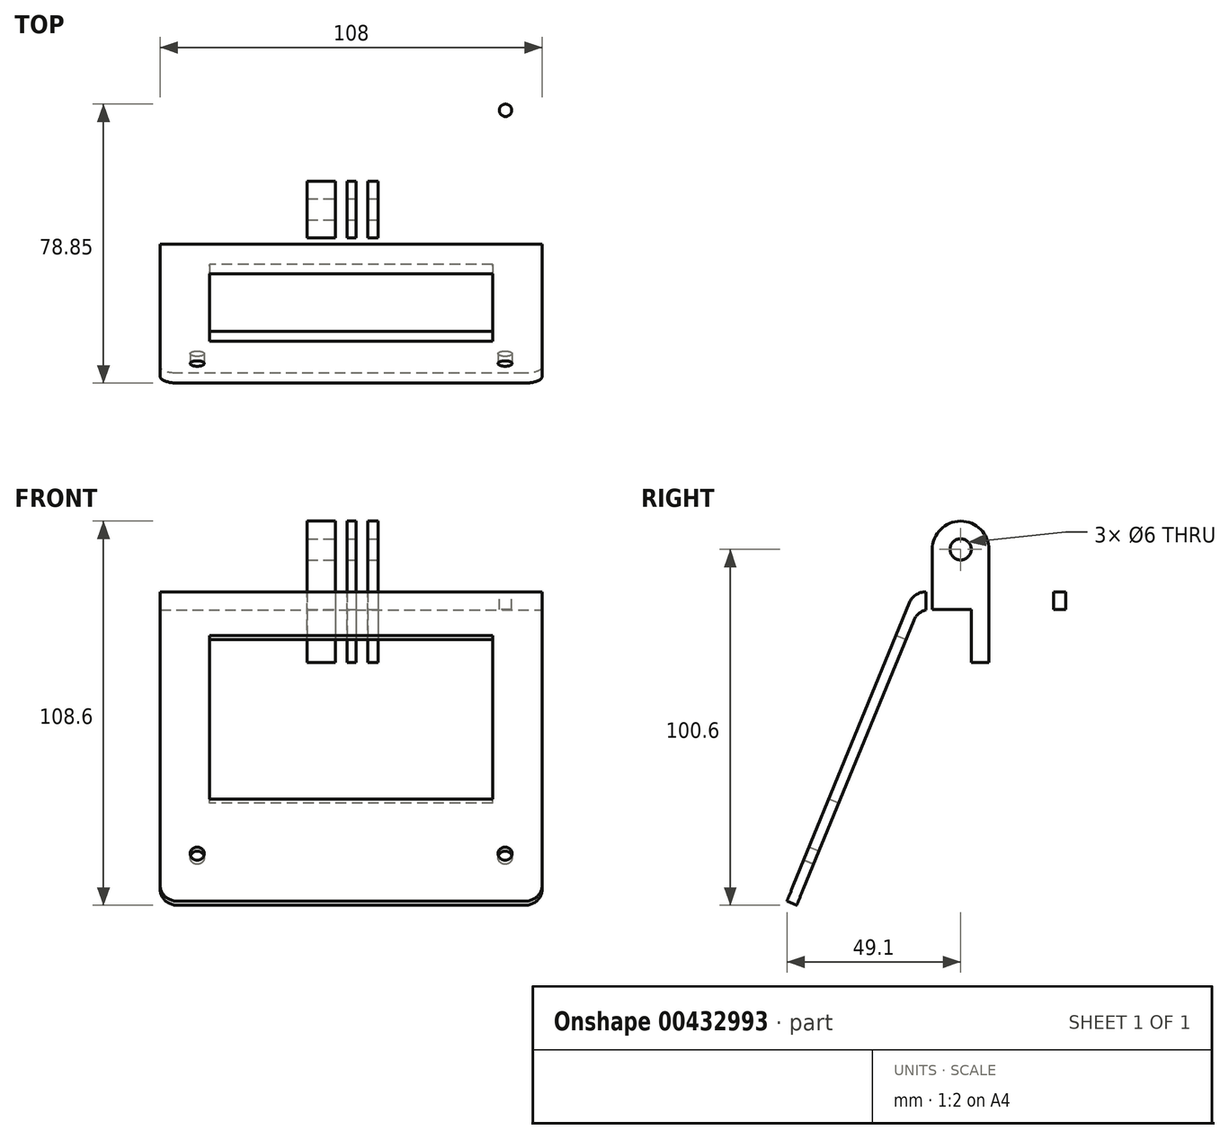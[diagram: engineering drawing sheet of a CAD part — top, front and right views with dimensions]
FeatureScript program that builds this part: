
annotation { "Feature Type Name" : "Feature", "Feature Type Description" : "" }
export const myFeature = defineFeature(function(context is Context, id is Id, definition is map)
    precondition{}
    {
        {
            var Q0;
            Q0=qCreatedBy(makeId("Top.planeOp"),FACE);
            var sketch = newSketch(context, id + "F0", { "sketchPlane" : qUnion([Q0])});
            skLineSegment(sketch, "E0.bottom", {"start": v(-54, 30) * mm, "end": v(-32.5, 30) * mm});
            skLineSegment(sketch, "E0.top", {"start": v(-54, 0) * mm, "end": v(-32.5, 0) * mm});
            skLineSegment(sketch, "E0.left", {"start": v(-54, 30) * mm, "end": v(-54, 0) * mm});
            skLineSegment(sketch, "E0.right", {"start": v(-32.5, 30) * mm, "end": v(-32.5, 0) * mm});
            skLineSegment(sketch, "E1.bottom", {"start": v(32.5, 30) * mm, "end": v(54, 30) * mm});
            skLineSegment(sketch, "E1.top", {"start": v(32.5, 0) * mm, "end": v(54, 0) * mm});
            skLineSegment(sketch, "E1.left", {"start": v(54, 30) * mm, "end": v(54, 0) * mm});
            skLineSegment(sketch, "E1.right", {"start": v(32.5, 30) * mm, "end": v(32.5, 0) * mm});
            skLineSegment(sketch, "E2.bottom", {"start": v(-54, 0) * mm, "end": v(32.5, 0) * mm});
            skLineSegment(sketch, "E3.bottom", {"start": v(-54, 0) * mm, "end": v(54, 0) * mm});
            skLineSegment(sketch, "E3.top", {"start": v(-54, -20) * mm, "end": v(54, -20) * mm});
            skLineSegment(sketch, "E3.left", {"start": v(-54, 0) * mm, "end": v(-54, -20) * mm});
            skLineSegment(sketch, "E3.right", {"start": v(54, 0) * mm, "end": v(54, -20) * mm});
            skSolve(sketch);
        }
        {
            var Q0;
            Q0=makeQuery(id+"F0.imprint","IMPRINT",FACE,{"disambiguationData":[TD([[makeQuery(id+"F0.imprint","IMPRINT",EDGE,{"derivedFrom":sQuery(id+"F0.wireOp",EDGE,"E0.bottom")}),-1.0]])]});
            var Q1;
            Q1=makeQuery(id+"F0.imprint","IMPRINT",FACE,{"disambiguationData":[TD([[makeQuery(id+"F0.imprint","IMPRINT",EDGE,{"derivedFrom":sQuery(id+"F0.wireOp",EDGE,"E3.top")}),1.0]])]});
            var Q2;
            Q2=makeQuery(id+"F0.imprint","IMPRINT",FACE,{"disambiguationData":[TD([[makeQuery(id+"F0.imprint","IMPRINT",EDGE,{"derivedFrom":sQuery(id+"F0.wireOp",EDGE,"E1.bottom")}),-1.0]])]});
            extrude(context, id + "F1", {"entities" : qUnion([Q0, Q1, Q2]), "depth" : 5 * mm});
        }
        {
            var Q0;
            Q0=makeQuery(id+"F1.opExtrude","SWEPT_FACE",FACE,{"disambiguationData":[OSD([sQuery(id+"F0.wireOp",EDGE,"E0.left"),sQuery(id+"F0.wireOp",EDGE,"E3.left")])]});
            var sketch = newSketch(context, id + "F2", { "sketchPlane" : qUnion([Q0])});
            skLineSegment(sketch, "E4", {"start": v(20, 0) * mm, "end": v(54.33, -83.6) * mm});
            skLineSegment(sketch, "E5", {"start": v(54.33, -83.6) * mm, "end": v(57.1, -82.46) * mm});
            skLineSegment(sketch, "E6", {"start": v(57.1, -82.46) * mm, "end": v(21.2, 5) * mm});
            skLineSegment(sketch, "E7", {"start": v(21.2, 5) * mm, "end": v(20, 5) * mm});
            skSolve(sketch);
        }
        {
            var Q0;
            Q0=makeQuery(id+"F2.imprint","IMPRINT",FACE,{"disambiguationData":[TD([[makeQuery(id+"F2.imprint","IMPRINT",EDGE,{"derivedFrom":sQuery(id+"F2.wireOp",EDGE,"E4")}),1.0]])]});
            extrude(context, id + "F3", {"entities" : qUnion([Q0]), "operationType" : NewBodyOperationType.ADD, "oppositeDirection" : true, "depth" : 108 * mm});
        }
        {
            var Q0;
            Q0=makeQuery(id+"F3.opExtrude","SWEPT_FACE",FACE,{"disambiguationData":[OSD([sQuery(id+"F2.wireOp",EDGE,"E6")])]});
            var sketch = newSketch(context, id + "F4", { "sketchPlane" : qUnion([Q0])});
            skLineSegment(sketch, "E8", {"start": v(-64.47, -83.42) * mm, "end": v(61.14, -83.42) * mm, "construction": true});
            skCircle(sketch, "E9", {"center": v(-43.5, -83.42) * mm, "radius": 2 * mm});
            skCircle(sketch, "E10", {"center": v(43.5, -83.42) * mm, "radius": 2 * mm});
            skSolve(sketch);
        }
        {
            var Q0;
            Q0=makeQuery(id+"F4.imprint","IMPRINT",FACE,{"disambiguationData":[TD([[makeQuery(id+"F4.imprint","IMPRINT",EDGE,{"derivedFrom":sQuery(id+"F4.wireOp",EDGE,"E9")}),1.0]])]});
            var Q1;
            Q1=makeQuery(id+"F4.imprint","IMPRINT",FACE,{"disambiguationData":[TD([[makeQuery(id+"F4.imprint","IMPRINT",EDGE,{"derivedFrom":sQuery(id+"F4.wireOp",EDGE,"E10")}),1.0]])]});
            extrude(context, id + "F5", {"entities" : qUnion([Q0, Q1]), "operationType" : NewBodyOperationType.REMOVE, "oppositeDirection" : true, "depth" : 25 * mm});
        }
        {
            var Q0;
            Q0=makeQuery(id+"F3.boolean.opBoolean","MERGE",FACE,{"derivedFrom":[makeQuery(id+"F1.opExtrude","CAP_FACE",FACE,{"disambiguationData":[OSD([sQuery(id+"F0.wireOp",EDGE,"E0.bottom"),sQuery(id+"F0.wireOp",EDGE,"E0.left"),sQuery(id+"F0.wireOp",EDGE,"E0.right"),sQuery(id+"F0.wireOp",EDGE,"E1.bottom"),sQuery(id+"F0.wireOp",EDGE,"E1.left"),sQuery(id+"F0.wireOp",EDGE,"E1.right"),sQuery(id+"F0.wireOp",EDGE,"E3.bottom"),sQuery(id+"F0.wireOp",EDGE,"E3.top"),sQuery(id+"F0.wireOp",EDGE,"E3.left"),sQuery(id+"F0.wireOp",EDGE,"E3.right")])],"isStart":false}),makeQuery(id+"F3.opExtrude","SWEPT_FACE",FACE,{"disambiguationData":[OSD([sQuery(id+"F2.wireOp",EDGE,"E7")])]})]});
            var sketch = newSketch(context, id + "F6", { "sketchPlane" : qUnion([Q0])});
            skLineSegment(sketch, "E11.bottom", {"start": v(-20, 0) * mm, "end": v(20, 0) * mm});
            skLineSegment(sketch, "E11.top", {"start": v(-20, -21.2) * mm, "end": v(20, -21.2) * mm});
            skLineSegment(sketch, "E11.left", {"start": v(-20, 0) * mm, "end": v(-20, -21.2) * mm});
            skLineSegment(sketch, "E11.right", {"start": v(20, 0) * mm, "end": v(20, -21.2) * mm});
            skLineSegment(sketch, "E12.bottom", {"start": v(-20, 0) * mm, "end": v(-12.45, 0) * mm});
            skLineSegment(sketch, "E12.top", {"start": v(-20, -21.2) * mm, "end": v(-12.45, -21.2) * mm});
            skLineSegment(sketch, "E12.right", {"start": v(-12.45, 0) * mm, "end": v(-12.45, -21.2) * mm});
            skLineSegment(sketch, "E13.bottom", {"start": v(-12.45, 0) * mm, "end": v(-4.45, 0) * mm});
            skLineSegment(sketch, "E13.top", {"start": v(-12.45, -21.2) * mm, "end": v(-4.45, -21.2) * mm});
            skLineSegment(sketch, "E13.right", {"start": v(-4.45, 0) * mm, "end": v(-4.45, -21.2) * mm});
            skLineSegment(sketch, "E14.bottom", {"start": v(-4.45, 0) * mm, "end": v(-1.15, 0) * mm});
            skLineSegment(sketch, "E14.top", {"start": v(-4.45, -21.2) * mm, "end": v(-1.15, -21.2) * mm});
            skLineSegment(sketch, "E14.right", {"start": v(-1.15, 0) * mm, "end": v(-1.15, -21.2) * mm});
            skLineSegment(sketch, "E15.bottom", {"start": v(-1.15, 0) * mm, "end": v(1.35, 0) * mm});
            skLineSegment(sketch, "E15.top", {"start": v(-1.15, -21.2) * mm, "end": v(1.35, -21.2) * mm});
            skLineSegment(sketch, "E15.right", {"start": v(1.35, 0) * mm, "end": v(1.35, -21.2) * mm});
            skLineSegment(sketch, "E16.bottom", {"start": v(1.35, 0) * mm, "end": v(4.65, 0) * mm});
            skLineSegment(sketch, "E16.top", {"start": v(1.35, -21.2) * mm, "end": v(4.65, -21.2) * mm});
            skLineSegment(sketch, "E16.right", {"start": v(4.65, 0) * mm, "end": v(4.65, -21.2) * mm});
            skLineSegment(sketch, "E17.bottom", {"start": v(4.65, 0) * mm, "end": v(7.65, 0) * mm});
            skLineSegment(sketch, "E17.top", {"start": v(4.65, -21.2) * mm, "end": v(7.65, -21.2) * mm});
            skLineSegment(sketch, "E17.right", {"start": v(7.65, 0) * mm, "end": v(7.65, -21.2) * mm});
            skLineSegment(sketch, "E18.top", {"start": v(-20, -16) * mm, "end": v(20, -16) * mm});
            skLineSegment(sketch, "E18.left", {"start": v(-20, 0) * mm, "end": v(-20, -16) * mm});
            skLineSegment(sketch, "E18.right", {"start": v(20, 0) * mm, "end": v(20, -16) * mm});
            skSolve(sketch);
        }
        {
            var Q0;
            Q0=makeQuery(id+"F3.opExtrude","SWEPT_EDGE",EDGE,{"disambiguationData":[OSD([sQuery(id+"F2.wireOp",EDGE,"E6"),sQuery(id+"F2.wireOp",EDGE,"E7")])]});
            var Q1;
            {var subQ0=sQuery(id+"F0.wireOp",EDGE,"E3.top");Q1=makeQuery(id+"F3.boolean.opBoolean","MERGE",EDGE,{"derivedFrom":[makeQuery(id+"F1.opExtrude","CAP_EDGE",EDGE,{"disambiguationData":[OSD([subQ0])],"isStart":true}),makeQuery(id+"F3.opExtrude","SWEPT_EDGE",EDGE,{"disambiguationData":[OSD([sQuery(id+"F0.wireOp",EDGE,"E0.left"),subQ0,sQuery(id+"F0.wireOp",EDGE,"E3.left"),sQuery(id+"F2.wireOp",EDGE,"E4")])]})]});}
            var Q2;
            Q2=makeQuery(id+"F1.opExtrude","SWEPT_EDGE",EDGE,{"disambiguationData":[OSD([sQuery(id+"F0.wireOp",EDGE,"E0.bottom"),sQuery(id+"F0.wireOp",EDGE,"E0.left")])]});
            var Q3;
            Q3=makeQuery(id+"F1.opExtrude","SWEPT_EDGE",EDGE,{"disambiguationData":[OSD([sQuery(id+"F0.wireOp",EDGE,"E1.bottom"),sQuery(id+"F0.wireOp",EDGE,"E1.left")])]});
            var Q4;
            Q4=makeQuery(id+"F3.opExtrude","CAP_EDGE",EDGE,{"disambiguationData":[OSD([sQuery(id+"F2.wireOp",EDGE,"E5")])],"isStart":false});
            var Q5;
            Q5=makeQuery(id+"F3.opExtrude","CAP_EDGE",EDGE,{"disambiguationData":[OSD([sQuery(id+"F2.wireOp",EDGE,"E5")])],"isStart":true});
            var Q6;
            Q6=makeQuery(id+"F1.opExtrude","SWEPT_EDGE",EDGE,{"disambiguationData":[OSD([sQuery(id+"F0.wireOp",EDGE,"E0.right"),sQuery(id+"F0.wireOp",EDGE,"E3.bottom")])]});
            var Q7;
            Q7=makeQuery(id+"F1.opExtrude","SWEPT_EDGE",EDGE,{"disambiguationData":[OSD([sQuery(id+"F0.wireOp",EDGE,"E1.right"),sQuery(id+"F0.wireOp",EDGE,"E3.bottom")])]});
            fillet(context, id + "F7", {"entities" : qUnion([Q0, Q1, Q2, Q3, Q4, Q5, Q6, Q7]), "radius" : 5 * mm, "tangentPropagation" : true, "allowEdgeOverflow" : false});
        }
        {
            var Q0;
            {var subQ0=sQuery(id+"F6.wireOp",EDGE,"E11.bottom");var subQ1=sQuery(id+"F6.wireOp",EDGE,"E12.right");var subQ2=makeQuery(id+"F6.imprint","INTERSECT",VERTEX,{"derivedFrom":[subQ1,subQ0]});Q0=makeQuery(id+"F6.imprint","IMPRINT",FACE,{"disambiguationData":[TD([[makeQuery(id+"F6.imprint","IMPRINT",EDGE,{"disambiguationData":[TD([[subQ2,-1.0]])],"derivedFrom":subQ1}),1.0]])]});}
            var Q1;
            {var subQ0=sQuery(id+"F6.wireOp",EDGE,"E11.bottom");var subQ1=sQuery(id+"F6.wireOp",EDGE,"E14.right");var subQ2=makeQuery(id+"F6.imprint","INTERSECT",VERTEX,{"derivedFrom":[subQ1,subQ0]});Q1=makeQuery(id+"F6.imprint","IMPRINT",FACE,{"disambiguationData":[TD([[makeQuery(id+"F6.imprint","IMPRINT",EDGE,{"disambiguationData":[TD([[subQ2,-1.0]])],"derivedFrom":subQ1}),1.0]])]});}
            var Q2;
            {var subQ0=sQuery(id+"F6.wireOp",EDGE,"E11.bottom");var subQ1=sQuery(id+"F6.wireOp",EDGE,"E16.right");var subQ2=makeQuery(id+"F6.imprint","INTERSECT",VERTEX,{"derivedFrom":[subQ1,subQ0]});Q2=makeQuery(id+"F6.imprint","IMPRINT",FACE,{"disambiguationData":[TD([[makeQuery(id+"F6.imprint","IMPRINT",EDGE,{"disambiguationData":[TD([[subQ2,-1.0]])],"derivedFrom":subQ1}),1.0]])]});}
            extrude(context, id + "F8", {"entities" : qUnion([Q0, Q1, Q2]), "operationType" : NewBodyOperationType.ADD, "depth" : 20 * mm});
        }
        {
            var Q0;
            {var subQ0=sQuery(id+"F6.wireOp",EDGE,"E18.top");Q0=makeQuery(id+"F8.opExtrude","CAP_EDGE",EDGE,{"disambiguationData":[OSD([subQ0]),TDD([makeQuery(id+"F6.imprint","IMPRINT",EDGE,{"disambiguationData":[TD([[makeQuery(id+"F6.imprint","INTERSECT",VERTEX,{"derivedFrom":[sQuery(id+"F6.wireOp",EDGE,"E12.right"),subQ0]}),-1.0]])],"derivedFrom":subQ0})])],"isStart":false});}
            var Q1;
            {var subQ0=sQuery(id+"F6.wireOp",EDGE,"E18.top");Q1=makeQuery(id+"F8.opExtrude","CAP_EDGE",EDGE,{"disambiguationData":[OSD([subQ0]),TDD([makeQuery(id+"F6.imprint","IMPRINT",EDGE,{"disambiguationData":[TD([[makeQuery(id+"F6.imprint","INTERSECT",VERTEX,{"derivedFrom":[sQuery(id+"F6.wireOp",EDGE,"E14.right"),subQ0]}),-1.0]])],"derivedFrom":subQ0})])],"isStart":false});}
            var Q2;
            {var subQ0=sQuery(id+"F6.wireOp",EDGE,"E18.top");Q2=makeQuery(id+"F8.opExtrude","CAP_EDGE",EDGE,{"disambiguationData":[OSD([subQ0]),TDD([makeQuery(id+"F6.imprint","IMPRINT",EDGE,{"disambiguationData":[TD([[makeQuery(id+"F6.imprint","INTERSECT",VERTEX,{"derivedFrom":[sQuery(id+"F6.wireOp",EDGE,"E16.right"),subQ0]}),-1.0]])],"derivedFrom":subQ0})])],"isStart":false});}
            var Q3;
            {var subQ0=sQuery(id+"F6.wireOp",EDGE,"E11.bottom");Q3=makeQuery(id+"F8.opExtrude","CAP_EDGE",EDGE,{"disambiguationData":[OSD([subQ0]),TDD([makeQuery(id+"F6.imprint","IMPRINT",EDGE,{"disambiguationData":[TD([[makeQuery(id+"F6.imprint","INTERSECT",VERTEX,{"derivedFrom":[sQuery(id+"F6.wireOp",EDGE,"E12.right"),subQ0]}),-1.0]])],"derivedFrom":subQ0})])],"isStart":false});}
            var Q4;
            {var subQ0=sQuery(id+"F6.wireOp",EDGE,"E11.bottom");Q4=makeQuery(id+"F8.opExtrude","CAP_EDGE",EDGE,{"disambiguationData":[OSD([subQ0]),TDD([makeQuery(id+"F6.imprint","IMPRINT",EDGE,{"disambiguationData":[TD([[makeQuery(id+"F6.imprint","INTERSECT",VERTEX,{"derivedFrom":[sQuery(id+"F6.wireOp",EDGE,"E14.right"),subQ0]}),-1.0]])],"derivedFrom":subQ0})])],"isStart":false});}
            var Q5;
            {var subQ0=sQuery(id+"F6.wireOp",EDGE,"E11.bottom");Q5=makeQuery(id+"F8.opExtrude","CAP_EDGE",EDGE,{"disambiguationData":[OSD([subQ0]),TDD([makeQuery(id+"F6.imprint","IMPRINT",EDGE,{"disambiguationData":[TD([[makeQuery(id+"F6.imprint","INTERSECT",VERTEX,{"derivedFrom":[sQuery(id+"F6.wireOp",EDGE,"E16.right"),subQ0]}),-1.0]])],"derivedFrom":subQ0})])],"isStart":false});}
            fillet(context, id + "F9", {"entities" : qUnion([Q0, Q1, Q2, Q3, Q4, Q5]), "radius" : 8 * mm, "tangentPropagation" : true, "allowEdgeOverflow" : false});
        }
        {
            var Q0;
            Q0=makeQuery(id+"F8.opExtrude","SWEPT_FACE",FACE,{"disambiguationData":[OSD([sQuery(id+"F6.wireOp",EDGE,"E17.right")])]});
            var sketch = newSketch(context, id + "F10", { "sketchPlane" : qUnion([Q0])});
            skCircle(sketch, "E19", {"center": v(-8, 17) * mm, "radius": 3 * mm});
            skSolve(sketch);
        }
        {
            var Q0;
            Q0=makeQuery(id+"F10.imprint","IMPRINT",FACE,{"disambiguationData":[TD([[makeQuery(id+"F10.imprint","IMPRINT",EDGE,{"derivedFrom":sQuery(id+"F10.wireOp",EDGE,"E19")}),1.0]])]});
            extrude(context, id + "F11", {"entities" : qUnion([Q0]), "operationType" : NewBodyOperationType.REMOVE, "oppositeDirection" : true, "depth" : 40 * mm});
        }
        {
            var Q0;
            Q0=makeQuery(id+"F3.opExtrude","SWEPT_FACE",FACE,{"disambiguationData":[OSD([sQuery(id+"F2.wireOp",EDGE,"E6")])]});
            var sketch = newSketch(context, id + "F12", { "sketchPlane" : qUnion([Q0])});
            skLineSegment(sketch, "E20.bottom", {"start": v(-40, -16.78) * mm, "end": v(40, -16.78) * mm});
            skLineSegment(sketch, "E20.top", {"start": v(-40, -66.78) * mm, "end": v(40, -66.78) * mm});
            skLineSegment(sketch, "E20.left", {"start": v(-40, -16.78) * mm, "end": v(-40, -66.78) * mm});
            skLineSegment(sketch, "E20.right", {"start": v(40, -16.78) * mm, "end": v(40, -66.78) * mm});
            skSolve(sketch);
        }
        {
            var Q0;
            Q0=makeQuery(id+"F12.imprint","IMPRINT",FACE,{"disambiguationData":[TD([[makeQuery(id+"F12.imprint","IMPRINT",EDGE,{"derivedFrom":sQuery(id+"F12.wireOp",EDGE,"E20.bottom")}),-1.0]])]});
            extrude(context, id + "F13", {"entities" : qUnion([Q0]), "operationType" : NewBodyOperationType.REMOVE, "oppositeDirection" : true, "depth" : 25 * mm});
        }
        {
            var Q0;
            Q0=makeQuery(id+"F1.opExtrude","CAP_FACE",FACE,{"disambiguationData":[OSD([sQuery(id+"F0.wireOp",EDGE,"E0.bottom"),sQuery(id+"F0.wireOp",EDGE,"E0.left"),sQuery(id+"F0.wireOp",EDGE,"E0.right"),sQuery(id+"F0.wireOp",EDGE,"E1.bottom"),sQuery(id+"F0.wireOp",EDGE,"E1.left"),sQuery(id+"F0.wireOp",EDGE,"E1.right"),sQuery(id+"F0.wireOp",EDGE,"E3.bottom"),sQuery(id+"F0.wireOp",EDGE,"E3.top"),sQuery(id+"F0.wireOp",EDGE,"E3.left"),sQuery(id+"F0.wireOp",EDGE,"E3.right")])],"isStart":true});
            var sketch = newSketch(context, id + "F14", { "sketchPlane" : qUnion([Q0])});
            skLineSegment(sketch, "E21.bottom", {"start": v(-54, 0) * mm, "end": v(54, 0) * mm});
            skLineSegment(sketch, "E21.top", {"start": v(-54, 5) * mm, "end": v(54, 5) * mm});
            skLineSegment(sketch, "E21.left", {"start": v(-54, 0) * mm, "end": v(-54, 5) * mm});
            skLineSegment(sketch, "E21.right", {"start": v(54, 0) * mm, "end": v(54, 5) * mm});
            skSolve(sketch);
        }
        {
            var Q0;
            Q0=makeQuery(id+"F14.imprint","IMPRINT",FACE,{"disambiguationData":[TD([[makeQuery(id+"F14.imprint","IMPRINT",EDGE,{"derivedFrom":sQuery(id+"F14.wireOp",EDGE,"E21.top")}),-1.0]])]});
            extrude(context, id + "F15", {"entities" : qUnion([Q0]), "operationType" : NewBodyOperationType.ADD, "depth" : 15 * mm});
        }
        {
            var Q0;
            Q0=makeQuery(id+"F15.opExtrude","CAP_EDGE",EDGE,{"disambiguationData":[OSD([sQuery(id+"F14.wireOp",EDGE,"E21.right")])],"isStart":false});
            var Q1;
            Q1=makeQuery(id+"F15.opExtrude","CAP_EDGE",EDGE,{"disambiguationData":[OSD([sQuery(id+"F14.wireOp",EDGE,"E21.left")])],"isStart":false});
            fillet(context, id + "F16", {"entities" : qUnion([Q0, Q1]), "radius" : 5 * mm, "tangentPropagation" : true, "allowEdgeOverflow" : false});
        }
        {
            var Q0;
            Q0=makeQuery(id+"F3.boolean.opBoolean","MERGE",FACE,{"derivedFrom":[makeQuery(id+"F1.opExtrude","CAP_FACE",FACE,{"disambiguationData":[OSD([sQuery(id+"F0.wireOp",EDGE,"E0.bottom"),sQuery(id+"F0.wireOp",EDGE,"E0.left"),sQuery(id+"F0.wireOp",EDGE,"E0.right"),sQuery(id+"F0.wireOp",EDGE,"E1.bottom"),sQuery(id+"F0.wireOp",EDGE,"E1.left"),sQuery(id+"F0.wireOp",EDGE,"E1.right"),sQuery(id+"F0.wireOp",EDGE,"E3.bottom"),sQuery(id+"F0.wireOp",EDGE,"E3.top"),sQuery(id+"F0.wireOp",EDGE,"E3.left"),sQuery(id+"F0.wireOp",EDGE,"E3.right")])],"isStart":false}),makeQuery(id+"F3.opExtrude","SWEPT_FACE",FACE,{"disambiguationData":[OSD([sQuery(id+"F2.wireOp",EDGE,"E7")])]})]});
            var sketch = newSketch(context, id + "F17", { "sketchPlane" : qUnion([Q0])});
            skCircle(sketch, "E22", {"center": v(-43.61, 20) * mm, "radius": 1.75 * mm});
            skCircle(sketch, "E23.MirrorC", {"center": v(43.61, 20) * mm, "radius": 1.75 * mm});
            skSolve(sketch);
        }
        {
            var Q0;
            Q0=makeQuery(id+"F17.imprint","IMPRINT",FACE,{"disambiguationData":[TD([[makeQuery(id+"F17.imprint","IMPRINT",EDGE,{"derivedFrom":sQuery(id+"F17.wireOp",EDGE,"E22")}),1.0]])]});
            var Q1;
            Q1=makeQuery(id+"F17.imprint","IMPRINT",FACE,{"disambiguationData":[TD([[makeQuery(id+"F17.imprint","IMPRINT",EDGE,{"derivedFrom":sQuery(id+"F17.wireOp",EDGE,"E23.MirrorC")}),-1.0]])]});
            extrude(context, id + "F18", {"entities" : qUnion([Q0, Q1]), "operationType" : NewBodyOperationType.REMOVE, "oppositeDirection" : true, "depth" : 25 * mm});
        }
    });
